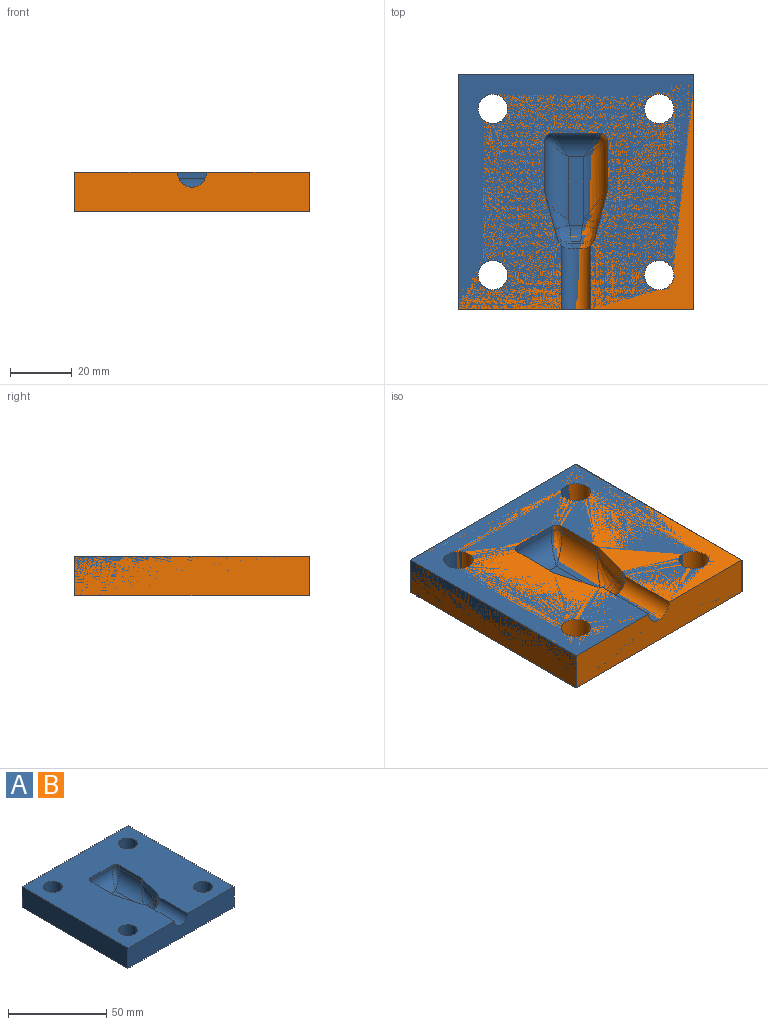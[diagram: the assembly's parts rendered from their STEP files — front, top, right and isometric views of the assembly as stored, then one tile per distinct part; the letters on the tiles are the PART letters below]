
ASSEMBLY  parts=2 mates=1
PART A: 37 faces, bbox 77x77x17.1 mm
  f0: plane 76.62x76.62mm, normal (0,0,1), area 4668.2mm2, adj f1,f2,f3,f4,f5,f7,f8,f9
  f1: cylinder r=4.76mm len=20.65mm, axis (0,-1,0), area 301.6mm2, adj f0,f2,f22,f23,f27
  f2: plane 76.2x12.7mm, normal (0,-1,0), area 932.1mm2, adj f0,f1,f3,f5,f6
  f3: plane 76.2x12.7mm, normal (1,0,0), area 967.7mm2, adj f0,f2,f4,f6
  f4: plane 76.2x12.7mm, normal (0,1,0), area 967.7mm2, adj f0,f3,f5,f6
  f5: plane 76.2x12.7mm, normal (-1,0,0), area 967.7mm2, adj f0,f2,f4,f6
  f6: plane 76.2x76.2mm, normal (0,0,-1), area 5521.4mm2, adj f2,f3,f4,f5,f33,f34,f35,f36
  f7: plane 15.84x1.91mm, normal (-1,0,0), area 30.2mm2, adj f0,f13,f17,f32
  f8: plane 15.24x1.91mm, normal (0,-1,0), area 29mm2, adj f0,f13,f14,f18
  f9: plane 16.51x1.91mm, normal (1,0,0), area 31.5mm2, adj f0,f11,f14,f21
  f10: plane 22.24x5.08mm, normal (0,0,1), area 112mm2, adj f17,f18,f19,f21,f25,f30
  f11: plane 16.09x5.26mm, normal (0.97,0.26,0), area 66.1mm2, adj f0,f9,f21,f23,f24,f25,f26
  f12: plane 14.64x4.45mm, normal (-0.97,0.26,0), area 59.2mm2, adj f0,f27,f28,f29,f30,f31,f32
  f13: cylinder r=2.54mm len=2.54mm, axis (0,0,-1), area 7.6mm2, adj f0,f7,f8,f16
  f14: cylinder r=2.54mm len=2.54mm, axis (0,0,1), area 7.6mm2, adj f0,f8,f9,f20
  f15: plane 3.08x0.62mm, normal (0,0.71,0.71), area 2.5mm2, adj f19,f22,f24,f28
  f16: bspline ~8.94x7.62mm, area 21mm2, adj f13,f17,f18
  f17: cylinder r=7.62mm len=25.37mm, axis (0,1,0), area 216.2mm2, adj f7,f10,f16,f31
  f18: cylinder r=7.62mm len=15.24mm, axis (-1,0,0), area 121.6mm2, adj f8,f10,f16,f20
  f19: cylinder r=7.62mm len=5.39mm, axis (-1,0,0), area 21.3mm2, adj f10,f15,f26,f29
  f20: bspline ~8.94x7.62mm, area 21mm2, adj f14,f18,f21
  f21: cylinder r=7.62mm len=25.37mm, axis (0,-1,0), area 218.5mm2, adj f9,f10,f11,f20,f25
  f22: cylinder r=7.62mm len=2.75mm, axis (1,0,0), area 6.4mm2, adj f1,f15,f23,f27
  f23: bspline ~9.25x5.11mm, area 30.5mm2, adj f0,f1,f11,f22,f24
  f24: cylinder r=5.08mm len=5.07mm, axis (0.19,-0.69,0.69), area 6.3mm2, adj f11,f15,f23,f26
  f25: cylinder r=5.08mm len=11.8mm, axis (0.26,-0.97,0), area 51.4mm2, adj f10,f11,f21,f26
  f26: bspline ~7.93x6.28mm, area 33.3mm2, adj f11,f19,f24,f25
  f27: bspline ~11.15x5.2mm, area 30.5mm2, adj f0,f1,f12,f22,f28
  f28: cylinder r=5.08mm len=5.07mm, axis (-0.19,-0.69,0.69), area 6.3mm2, adj f12,f15,f27,f29
  f29: bspline ~7.93x6.28mm, area 33.3mm2, adj f12,f19,f28,f30
  f30: cylinder r=5.08mm len=5.43mm, axis (-0.26,-0.97,0), area 16.1mm2, adj f10,f12,f29,f31
  f31: bspline ~10.83x7.62mm, area 59.9mm2, adj f12,f17,f30,f32
  f32: cylinder r=5.08mm len=1.91mm, axis (0,0,-1), area 2.5mm2, adj f0,f7,f12,f31
  f33: cylinder r=4.76mm len=12.7mm, axis (0,0,1), area 380mm2, adj f0,f6
  f34: cylinder r=4.76mm len=12.7mm, axis (0,0,1), area 380mm2, adj f0,f6
  f35: cylinder r=4.76mm len=12.7mm, axis (0,0,1), area 380mm2, adj f0,f6
  f36: cylinder r=4.76mm len=12.7mm, axis (0,0,1), area 380mm2, adj f0,f6
PART B: same geometry as A
PLACE A t=(62.51,108.37,-174.74)mm
PLACE B t=(62.51,108.37,-174.74)mm
MATE fastened B.f0 <-> A.f0  axis (0,0,1) through (24.41,108.37,-162.04)mm
